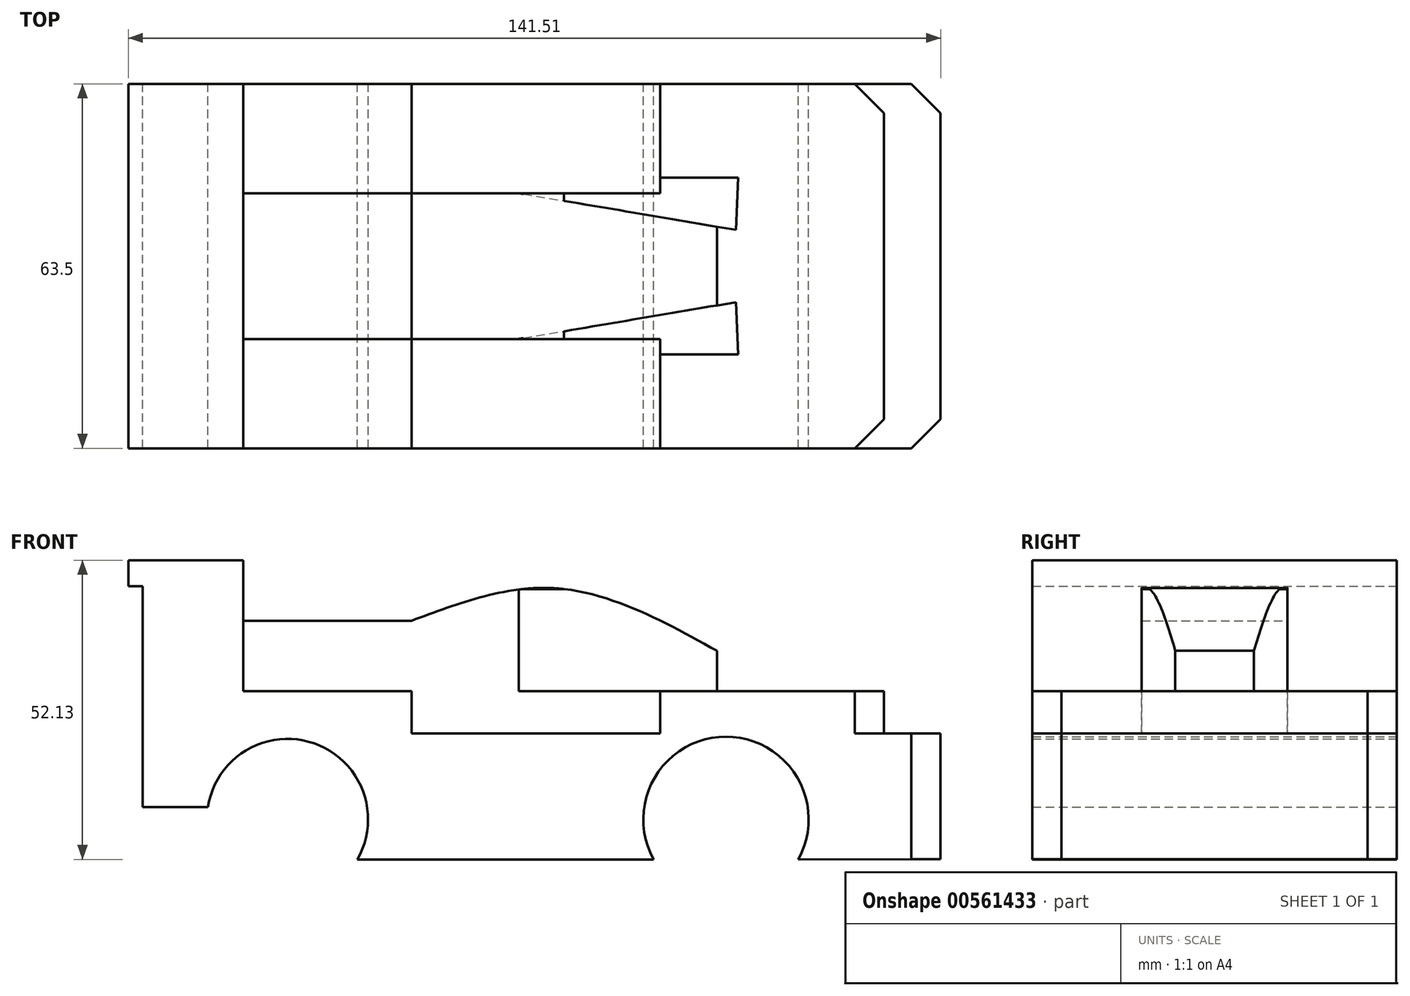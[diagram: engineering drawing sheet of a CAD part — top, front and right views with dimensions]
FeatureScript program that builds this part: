
annotation { "Feature Type Name" : "Feature", "Feature Type Description" : "" }
export const myFeature = defineFeature(function(context is Context, id is Id, definition is map)
    precondition{}
    {
        {
            var Q0;
            Q0=qCreatedBy(makeId("Front.planeOp"),FACE);
            var sketch = newSketch(context, id + "F0", { "sketchPlane" : qUnion([Q0])});
            skLineSegment(sketch, "E0", {"start": v(-54.75, 5.02) * mm, "end": v(-54.75, -37.98) * mm});
            skLineSegment(sketch, "E1", {"start": v(-54.75, 5.02) * mm, "end": v(-37.22, 5.02) * mm});
            skLineSegment(sketch, "E2", {"start": v(-37.22, 5.02) * mm, "end": v(-37.22, -17.77) * mm});
            skLineSegment(sketch, "E3", {"start": v(-37.22, -17.77) * mm, "end": v(-7.88, -17.77) * mm});
            skLineSegment(sketch, "E4", {"start": v(-7.88, -17.77) * mm, "end": v(-7.88, -25.18) * mm});
            skLineSegment(sketch, "E5", {"start": v(-7.88, -25.18) * mm, "end": v(35.44, -25.18) * mm});
            skLineSegment(sketch, "E6", {"start": v(35.44, -25.18) * mm, "end": v(35.44, -17.77) * mm});
            skLineSegment(sketch, "E7", {"start": v(35.44, -17.77) * mm, "end": v(74.43, -17.77) * mm});
            skLineSegment(sketch, "E8", {"start": v(74.43, -17.77) * mm, "end": v(74.43, -25.18) * mm});
            skLineSegment(sketch, "E9", {"start": v(74.43, -25.18) * mm, "end": v(84.32, -25.18) * mm});
            skLineSegment(sketch, "E10", {"start": v(84.32, -25.18) * mm, "end": v(84.32, -47.08) * mm});
            skLineSegment(sketch, "E11.bottom", {"start": v(-37.22, -5.53) * mm, "end": v(-7.88, -5.53) * mm});
            skLineSegment(sketch, "E11.left", {"start": v(-37.22, -5.53) * mm, "end": v(-37.22, -17.77) * mm});
            skLineSegment(sketch, "E11.right", {"start": v(-7.88, -5.53) * mm, "end": v(-7.88, -17.77) * mm});
            skLineSegment(sketch, "E12.left", {"start": v(-7.88, -14.76) * mm, "end": v(-7.88, -17.77) * mm});
            skLineSegment(sketch, "E12.right", {"start": v(35.44, -17.77) * mm, "end": v(35.44, -17.77) * mm});
            skCircle(sketch, "E13", {"center": v(-29.47, -40.14) * mm, "radius": 14.03 * mm});
            skCircle(sketch, "E14", {"center": v(46.92, -40.14) * mm, "radius": 14.4 * mm});
            skLineSegment(sketch, "E15", {"start": v(-17.3, -47.11) * mm, "end": v(34.31, -47.11) * mm});
            skLineSegment(sketch, "E16.bottom", {"start": v(-54.75, 5.02) * mm, "end": v(-57.2, 5.02) * mm});
            skLineSegment(sketch, "E16.top", {"start": v(-54.75, 0.52) * mm, "end": v(-57.2, 0.52) * mm});
            skLineSegment(sketch, "E16.left", {"start": v(-54.75, 5.02) * mm, "end": v(-54.75, 0.52) * mm});
            skLineSegment(sketch, "E16.right", {"start": v(-57.2, 5.02) * mm, "end": v(-57.2, 0.52) * mm});
            skLineSegment(sketch, "E17", {"start": v(59.53, -47.11) * mm, "end": v(84.32, -47.08) * mm});
            skLineSegment(sketch, "E18", {"start": v(-54.75, -37.98) * mm, "end": v(-43.34, -37.98) * mm});
            skFitSpline(sketch, "E19", {"points": [v(-7.88, -5.53) * mm, v(18.7, 0) * mm, v(45.34, -10.77) * mm], "startDerivative": vector(48.15, 17.54) * mm, "endDerivative": vector(36.89, -20.3) * mm});
            skLineSegment(sketch, "E20", {"start": v(45.34, -10.77) * mm, "end": v(45.34, -17.77) * mm});
            skSolve(sketch);
        }
        {
            var Q0;
            Q0=makeQuery(id+"F0.imprint","IMPRINT",FACE,{"disambiguationData":[TD([[makeQuery(id+"F0.imprint","IMPRINT",EDGE,{"derivedFrom":sQuery(id+"F0.wireOp",EDGE,"E0")}),1.0]])]});
            extrude(context, id + "F1", {"entities" : qUnion([Q0]), "endBound" : BoundingType.SYMMETRIC, "depth" : 63.5 * mm});
        }
        {
            var Q0;
            Q0=makeQuery(id+"F0.imprint","IMPRINT",FACE,{"disambiguationData":[TD([[makeQuery(id+"F0.imprint","IMPRINT",EDGE,{"derivedFrom":sQuery(id+"F0.wireOp",EDGE,"E4")}),1.0]])]});
            extrude(context, id + "F2", {"entities" : qUnion([Q0]), "operationType" : NewBodyOperationType.ADD, "endBound" : BoundingType.SYMMETRIC, "depth" : 25.4 * mm});
        }
        {
            var Q0;
            Q0=makeQuery(id+"F0.imprint","IMPRINT",FACE,{"disambiguationData":[TD([[makeQuery(id+"F0.imprint","IMPRINT",EDGE,{"derivedFrom":sQuery(id+"F0.wireOp",EDGE,"E11.bottom")}),-1.0]])]});
            extrude(context, id + "F3", {"entities" : qUnion([Q0]), "operationType" : NewBodyOperationType.ADD, "endBound" : BoundingType.SYMMETRIC, "depth" : 25.4 * mm});
        }
        {
            var Q0;
            Q0=makeQuery(id+"F0.imprint","IMPRINT",FACE,{"disambiguationData":[TD([[makeQuery(id+"F0.imprint","IMPRINT",EDGE,{"derivedFrom":sQuery(id+"F0.wireOp",EDGE,"E16.bottom")}),1.0]])]});
            extrude(context, id + "F4", {"entities" : qUnion([Q0]), "operationType" : NewBodyOperationType.ADD, "endBound" : BoundingType.SYMMETRIC, "depth" : 63.5 * mm});
        }
        {
            var Q0;
            Q0=makeQuery(id+"F1.opExtrude","CAP_EDGE",EDGE,{"disambiguationData":[OSD([sQuery(id+"F0.wireOp",EDGE,"E8")])],"isStart":false});
            var Q1;
            Q1=makeQuery(id+"F1.opExtrude","CAP_EDGE",EDGE,{"disambiguationData":[OSD([sQuery(id+"F0.wireOp",EDGE,"E8")])],"isStart":true});
            var Q2;
            Q2=makeQuery(id+"F1.opExtrude","CAP_EDGE",EDGE,{"disambiguationData":[OSD([sQuery(id+"F0.wireOp",EDGE,"E10")])],"isStart":true});
            var Q3;
            Q3=makeQuery(id+"F1.opExtrude","CAP_EDGE",EDGE,{"disambiguationData":[OSD([sQuery(id+"F0.wireOp",EDGE,"E10")])],"isStart":false});
            chamfer(context, id + "F5", {"entities" : qUnion([Q0, Q1, Q2, Q3]), "width" : 5.08 * mm, "tangentPropagation" : true});
        }
        {
            var Q0;
            Q0=qCreatedBy(makeId("Top.planeOp"),FACE);
            var sketch = newSketch(context, id + "F6", { "sketchPlane" : qUnion([Q0])});
            skLineSegment(sketch, "E21.bottom", {"start": v(7.54, -15.41) * mm, "end": v(49.02, -15.38) * mm});
            skLineSegment(sketch, "E21.top", {"start": v(7.45, -13.27) * mm, "end": v(48.66, -6.3) * mm});
            skLineSegment(sketch, "E21.left", {"start": v(7.54, -15.41) * mm, "end": v(7.45, -13.27) * mm});
            skLineSegment(sketch, "E21.right", {"start": v(49.02, -15.38) * mm, "end": v(48.66, -6.3) * mm});
            skLineSegment(sketch, "E22.MirrorCS", {"start": v(49.02, 15.38) * mm, "end": v(48.66, 6.3) * mm});
            skLineSegment(sketch, "E23.MirrorCS", {"start": v(7.54, 15.41) * mm, "end": v(49.02, 15.38) * mm});
            skLineSegment(sketch, "E24.MirrorCS", {"start": v(7.45, 13.27) * mm, "end": v(48.66, 6.3) * mm});
            skLineSegment(sketch, "E25.MirrorCS", {"start": v(7.54, 15.41) * mm, "end": v(7.45, 13.27) * mm});
            skSolve(sketch);
        }
        {
            var Q0;
            Q0=qSketchRegion(id+"F6",true);
            extrude(context, id + "F7", {"entities" : qUnion([Q0]), "operationType" : NewBodyOperationType.REMOVE, "oppositeDirection" : true, "depth" : 17.78 * mm});
        }
    });
